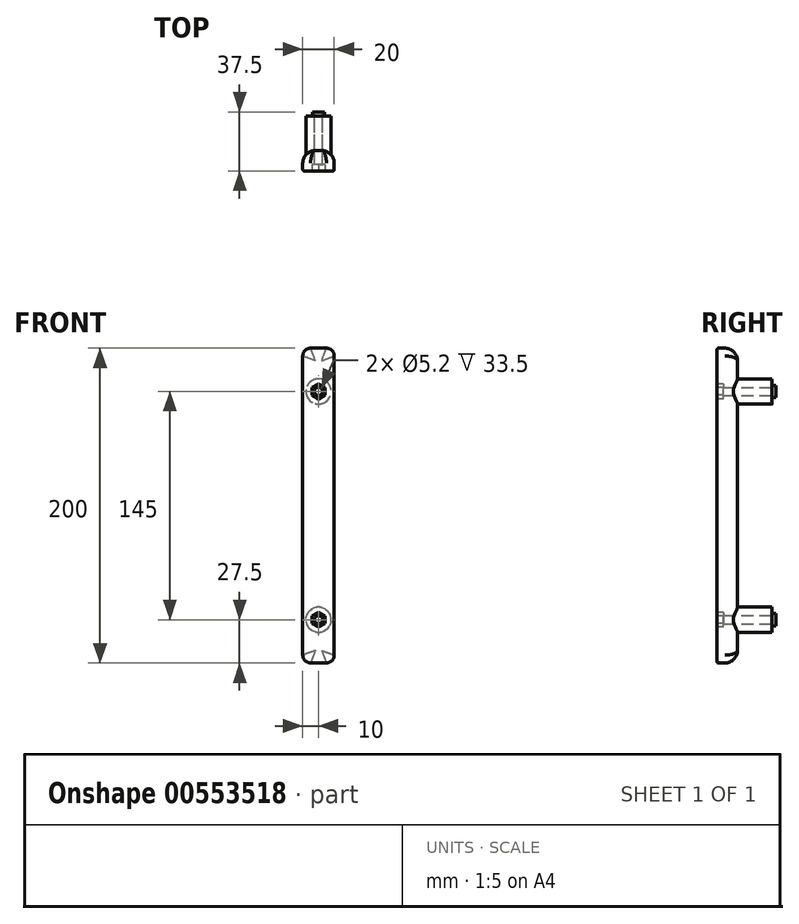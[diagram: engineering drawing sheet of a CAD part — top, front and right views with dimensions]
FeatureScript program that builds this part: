
annotation { "Feature Type Name" : "Feature", "Feature Type Description" : "" }
export const myFeature = defineFeature(function(context is Context, id is Id, definition is map)
    precondition{}
    {
        {
            var Q0;
            Q0=qCreatedBy(makeId("Front.planeOp"),FACE);
            var sketch = newSketch(context, id + "F0", { "sketchPlane" : qUnion([Q0])});
            skLineSegment(sketch, "E0.bottom", {"start": v(5, 0) * mm, "end": v(15, 0) * mm});
            skLineSegment(sketch, "E0.top", {"start": v(0, -100) * mm, "end": v(20, -100) * mm});
            skLineSegment(sketch, "E0.left", {"start": v(0, -5) * mm, "end": v(0, -100) * mm});
            skLineSegment(sketch, "E0.right", {"start": v(20, -5) * mm, "end": v(20, -100) * mm});
            skPoint(sketch, "E1.visualSharp", {"position": v(0, 0) * mm});
            skArc(sketch, "E1.filletArc", {"start": v(5, 0) * mm, "mid": v(1.46, -1.46) * mm, "end": v(0, -5) * mm});
            skPoint(sketch, "E2.visualSharp", {"position": v(20, 0) * mm});
            skArc(sketch, "E2.filletArc", {"start": v(20, -5) * mm, "mid": v(18.54, -1.46) * mm, "end": v(15, 0) * mm});
            skPoint(sketch, "E3.visualSharp", {"position": v(20, -100) * mm});
            skSolve(sketch);
        }
        {
            var Q0;
            Q0=makeQuery(id+"F0.imprint","IMPRINT",FACE,{"disambiguationData":[TD([[makeQuery(id+"F0.imprint","IMPRINT",EDGE,{"derivedFrom":sQuery(id+"F0.wireOp",EDGE,"E0.bottom")}),-1.0]])]});
            extrude(context, id + "F1", {"entities" : qUnion([Q0]), "depth" : 5 * mm, "offsetDistance" : 25 * mm});
        }
        {
            var Q0;
            {var subQ0=makeQuery(id+"F1.opExtrude","CAP_EDGE",EDGE,{"disambiguationData":[OSD([sQuery(id+"F0.wireOp",EDGE,"E0.right")])],"isStart":false});Q0=makeQuery(id+"F13.boolean.opBoolean","MERGE",EDGE,{"derivedFrom":[subQ0,makeQuery(id+"F13.opPattern","COPY",EDGE,{"derivedFrom":subQ0,"instanceName":"1"})]});}
            fillet(context, id + "F2", {"entities" : qUnion([Q0]), "radius" : 1 * mm, "tangentPropagation" : true, "allowEdgeOverflow" : false});
        }
        {
            var Q0;
            Q0=makeQuery(id+"F1.opExtrude","CAP_FACE",FACE,{"disambiguationData":[OSD([sQuery(id+"F0.wireOp",EDGE,"E0.bottom"),sQuery(id+"F0.wireOp",EDGE,"E0.top"),sQuery(id+"F0.wireOp",EDGE,"E0.left"),sQuery(id+"F0.wireOp",EDGE,"E0.right"),sQuery(id+"F0.wireOp",EDGE,"E1.filletArc"),sQuery(id+"F0.wireOp",EDGE,"E2.filletArc")])],"isStart":true});
            var sketch = newSketch(context, id + "F3", { "sketchPlane" : qUnion([Q0])});
            skCircle(sketch, "E4", {"center": v(-10, -27.5) * mm, "radius": 8 * mm});
            skLineSegment(sketch, "E5", {"start": v(-10, -27.5) * mm, "end": v(-10, -100) * mm, "construction": true});
            skSolve(sketch);
        }
        {
            var Q0;
            {var subQ0=makeQuery(id+"F1.opExtrude","CAP_FACE",FACE,{"disambiguationData":[OSD([sQuery(id+"F0.wireOp",EDGE,"E0.bottom"),sQuery(id+"F0.wireOp",EDGE,"E0.top"),sQuery(id+"F0.wireOp",EDGE,"E0.left"),sQuery(id+"F0.wireOp",EDGE,"E0.right"),sQuery(id+"F0.wireOp",EDGE,"E1.filletArc"),sQuery(id+"F0.wireOp",EDGE,"E2.filletArc")])],"isStart":true});Q0=makeQuery(id+"F13.boolean.opBoolean","MERGE",FACE,{"derivedFrom":[subQ0,makeQuery(id+"F13.opPattern","COPY",FACE,{"derivedFrom":subQ0,"instanceName":"1"})]});}
            extrude(context, id + "F4", {"entities" : qUnion([Q0]), "operationType" : NewBodyOperationType.ADD, "depth" : 8 * mm, "offsetDistance" : 25 * mm});
        }
        {
            var Q0;
            Q0=makeQuery(id+"F4.opExtrude","CAP_EDGE",EDGE,{"disambiguationData":[OSD([sQuery(id+"F0.wireOp",EDGE,"E0.left")])],"isStart":false});
            fillet(context, id + "F5", {"entities" : qUnion([Q0]), "radius" : 8 * mm, "tangentPropagation" : true, "allowEdgeOverflow" : false});
        }
        {
            var Q0;
            Q0=makeQuery(id+"F3.imprint","IMPRINT",FACE,{"disambiguationData":[TD([[makeQuery(id+"F3.imprint","IMPRINT",EDGE,{"derivedFrom":sQuery(id+"F3.wireOp",EDGE,"E4")}),1.0]])]});
            extrude(context, id + "F6", {"entities" : qUnion([Q0]), "operationType" : NewBodyOperationType.ADD, "depth" : 30 * mm, "offsetDistance" : 25 * mm});
        }
        {
            var Q0;
            Q0=makeQuery(id+"F6.opExtrude","CAP_FACE",FACE,{"disambiguationData":[OSD([sQuery(id+"F3.wireOp",EDGE,"E4")])],"isStart":false});
            var sketch = newSketch(context, id + "F7", { "sketchPlane" : qUnion([Q0])});
            skCircle(sketch, "E6", {"center": v(-10, -27.5) * mm, "radius": 3.85 * mm});
            skSolve(sketch);
        }
        {
            var Q0;
            Q0=makeQuery(id+"F7.imprint","IMPRINT",FACE,{"disambiguationData":[TD([[makeQuery(id+"F7.imprint","IMPRINT",EDGE,{"derivedFrom":sQuery(id+"F7.wireOp",EDGE,"E6")}),1.0]])]});
            extrude(context, id + "F8", {"entities" : qUnion([Q0]), "operationType" : NewBodyOperationType.ADD, "depth" : 2.5 * mm, "offsetDistance" : 25 * mm});
        }
        {
            var Q0;
            Q0=makeQuery(id+"F8.opExtrude","CAP_FACE",FACE,{"disambiguationData":[OSD([sQuery(id+"F7.wireOp",EDGE,"E6")])],"isStart":false});
            var sketch = newSketch(context, id + "F9", { "sketchPlane" : qUnion([Q0])});
            skCircle(sketch, "E7", {"center": v(-10, -27.5) * mm, "radius": 2.6 * mm});
            skSolve(sketch);
        }
        {
            var Q0;
            Q0=makeQuery(id+"F9.imprint","IMPRINT",FACE,{"disambiguationData":[TD([[makeQuery(id+"F9.imprint","IMPRINT",EDGE,{"derivedFrom":sQuery(id+"F9.wireOp",EDGE,"E7")}),1.0]])]});
            extrude(context, id + "F10", {"entities" : qUnion([Q0]), "operationType" : NewBodyOperationType.REMOVE, "endBound" : BoundingType.UP_TO_NEXT, "oppositeDirection" : true, "depth" : 25 * mm, "offsetDistance" : 25 * mm});
        }
        {
            var Q0;
            Q0=makeQuery(id+"F1.opExtrude","CAP_FACE",FACE,{"disambiguationData":[OSD([sQuery(id+"F0.wireOp",EDGE,"E0.bottom"),sQuery(id+"F0.wireOp",EDGE,"E0.top"),sQuery(id+"F0.wireOp",EDGE,"E0.left"),sQuery(id+"F0.wireOp",EDGE,"E0.right"),sQuery(id+"F0.wireOp",EDGE,"E1.filletArc"),sQuery(id+"F0.wireOp",EDGE,"E2.filletArc")])],"isStart":false});
            var sketch = newSketch(context, id + "F11", { "sketchPlane" : qUnion([Q0])});
            skCircle(sketch, "E8.cCircle", {"center": v(10, -27.5) * mm, "radius": 4.1 * mm, "construction": true});
            skLineSegment(sketch, "E8.0", {"start": v(5.9, -29.87) * mm, "end": v(5.9, -25.13) * mm});
            skLineSegment(sketch, "E8.1", {"start": v(5.9, -25.13) * mm, "end": v(10, -22.77) * mm});
            skLineSegment(sketch, "E8.2", {"start": v(10, -22.77) * mm, "end": v(14.1, -25.13) * mm});
            skLineSegment(sketch, "E8.3", {"start": v(14.1, -25.13) * mm, "end": v(14.1, -29.87) * mm});
            skLineSegment(sketch, "E8.4", {"start": v(14.1, -29.87) * mm, "end": v(10, -32.23) * mm});
            skLineSegment(sketch, "E8.5", {"start": v(10, -32.23) * mm, "end": v(5.9, -29.87) * mm});
            skPoint(sketch, "E8.0.midPoint", {"position": v(5.9, -27.5) * mm});
            skSolve(sketch);
        }
        {
            var Q0;
            Q0=makeQuery(id+"F11.imprint","IMPRINT",FACE,{"disambiguationData":[TD([[makeQuery(id+"F11.imprint","IMPRINT",EDGE,{"derivedFrom":sQuery(id+"F11.wireOp",EDGE,"E8.0")}),-1.0]])]});
            extrude(context, id + "F12", {"entities" : qUnion([Q0]), "operationType" : NewBodyOperationType.REMOVE, "oppositeDirection" : true, "depth" : 4 * mm, "offsetDistance" : 25 * mm});
        }
        {
            var Q0;
            Q0=makeQuery(id+"F1.opExtrude","SWEPT_BODY",BODY,{"disambiguationData":[OSD([sQuery(id+"F0.wireOp",EDGE,"E0.bottom"),sQuery(id+"F0.wireOp",EDGE,"E0.top"),sQuery(id+"F0.wireOp",EDGE,"E0.left"),sQuery(id+"F0.wireOp",EDGE,"E0.right"),sQuery(id+"F0.wireOp",EDGE,"E1.filletArc"),sQuery(id+"F0.wireOp",EDGE,"E2.filletArc")])]});
            var Q1;
            Q1=makeQuery(id+"F1.opExtrude","SWEPT_FACE",FACE,{"disambiguationData":[OSD([sQuery(id+"F0.wireOp",EDGE,"E0.top")])]});
            mirror(context, id + "F13", {"operationType" : NewBodyOperationType.ADD, "entities" : qUnion([Q0]), "mirrorPlane" : qUnion([Q1])});
        }
    });
